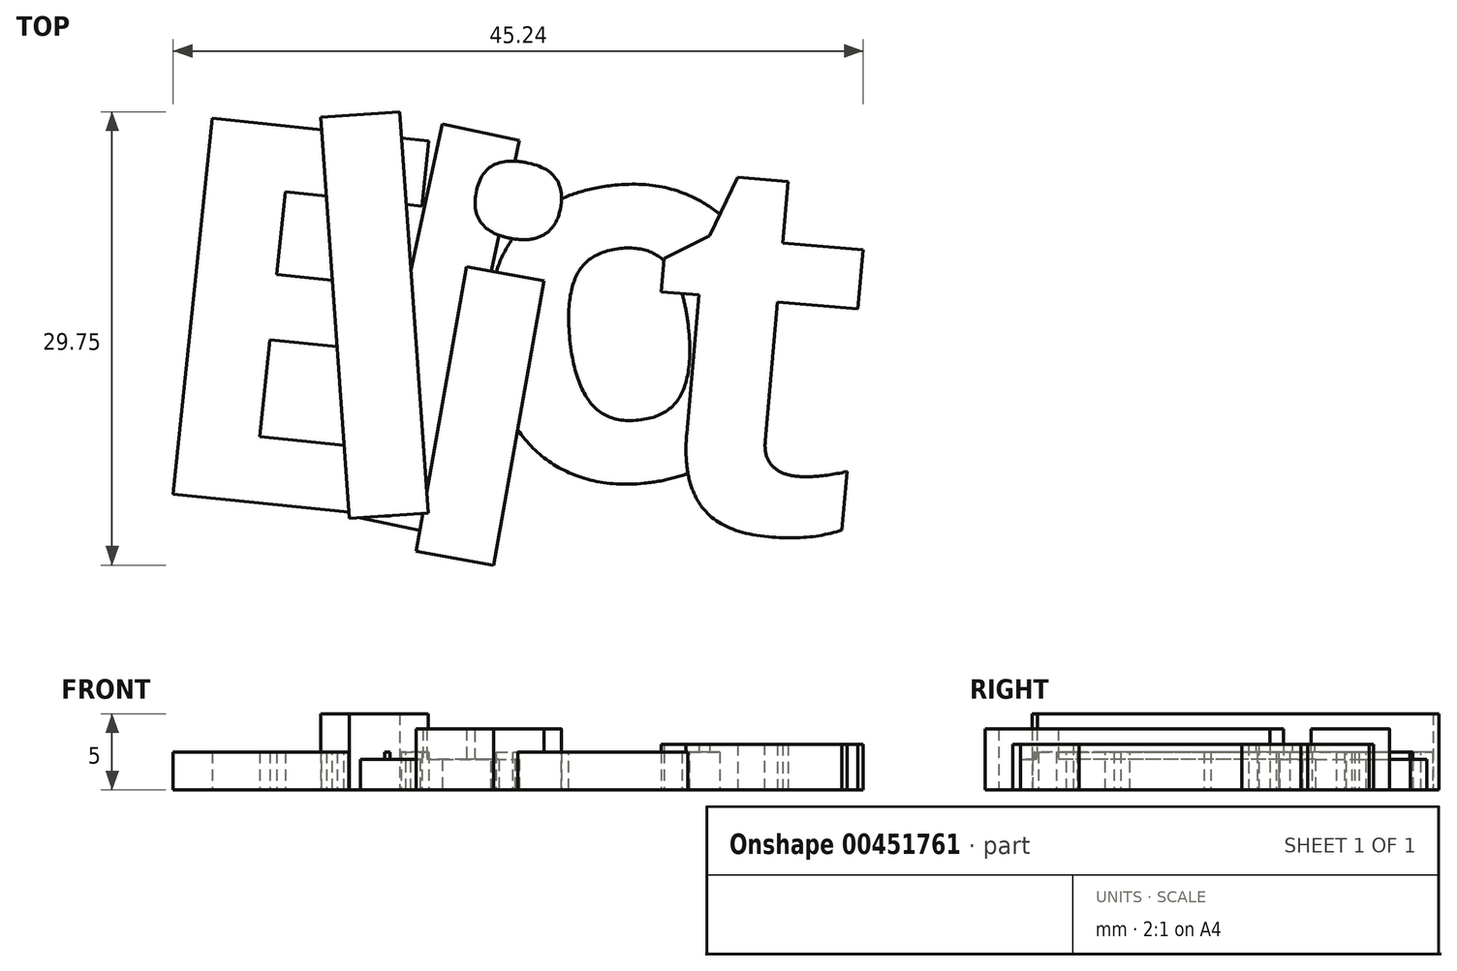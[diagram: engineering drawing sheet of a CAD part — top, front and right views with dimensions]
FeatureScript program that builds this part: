
annotation { "Feature Type Name" : "Feature", "Feature Type Description" : "" }
export const myFeature = defineFeature(function(context is Context, id is Id, definition is map)
    precondition{}
    {
        {
            var Q0;
            Q0=qCreatedBy(makeId("Top.planeOp"),FACE);
            var sketch = newSketch(context, id + "F0", { "sketchPlane" : qUnion([Q0])});
            skText(sketch, "E0", { "text": "E", "fontName": "OpenSans-Bold.ttf"});
            skText(sketch, "E1", { "text": "l", "fontName": "OpenSans-Bold.ttf"});
            skText(sketch, "E2", { "text": "i", "fontName": "OpenSans-Bold.ttf"});
            skText(sketch, "E3", { "text": "o", "fontName": "OpenSans-Bold.ttf"});
            skText(sketch, "E4", { "text": "t", "fontName": "OpenSans-Bold.ttf"});
            skLineSegment(sketch, "E5", {"start": v(-42.9, 49.18) * mm, "end": v(-72.08, 8.9) * mm, "construction": true});
            skLineSegment(sketch, "E6", {"start": v(-42.9, 49.18) * mm, "end": v(-73, 49.18) * mm, "construction": true});
            skText(sketch, "E7", { "text": "l", "fontName": "OpenSans-Bold.ttf"});
            const initialGuessF0  = {"E0": [-0.05238, -0.0083, 0.99466, -0.10322, 0.025], "E1": [-0.04043, -0.01042, 0.99747, 0.07107, 0.025], "E2": [-0.03602, -0.01192, 0.9848, -0.17365, 0.025], "E3": [-0.02907, -0.00869, 0.99452, 0.10453, 0.025], "E4": [-0.01939, -0.01029, 0.9962, -0.08716, 0.025], "E7": [-0.03979, -0.00958, 0.97815, -0.20791, 0.025]};
            skSetInitialGuess(sketch, initialGuessF0);
            skSolve(sketch);
        }
        {
            var Q0;
            {var subQ11=sQuery(id+"F0.wireOp",EDGE,"E0.sketch_text.stroke-1");Q0=makeQuery(id+"F0.imprint","IMPRINT",FACE,{"disambiguationData":[TD([[makeQuery(id+"F0.imprint","IMPRINT",EDGE,{"derivedFrom":subQ11}),-1.0]])]});}
            var Q1;
            {var subQ3=sQuery(id+"F0.wireOp",EDGE,"E1.sketch_text.stroke-3");var subQ9=sQuery(id+"F0.wireOp",EDGE,"E0.sketch_text.stroke-0");var subQ11=makeQuery(id+"F0.imprint","INTERSECT",VERTEX,{"derivedFrom":[subQ9,subQ3]});Q1=makeQuery(id+"F0.imprint","IMPRINT",FACE,{"disambiguationData":[TD([[makeQuery(id+"F0.imprint","IMPRINT",EDGE,{"disambiguationData":[TD([[subQ11,-1.0]])],"derivedFrom":subQ9}),-1.0]])]});}
            var Q2;
            {var subQ0=sQuery(id+"F0.wireOp",EDGE,"E0.sketch_text.stroke-7");Q2=makeQuery(id+"F0.imprint","IMPRINT",FACE,{"disambiguationData":[TD([[makeQuery(id+"F0.imprint","IMPRINT",EDGE,{"derivedFrom":subQ0}),-1.0]])]});}
            var Q3;
            {var subQ0=sQuery(id+"F0.wireOp",EDGE,"E0.sketch_text.stroke-3");Q3=makeQuery(id+"F0.imprint","IMPRINT",FACE,{"disambiguationData":[TD([[makeQuery(id+"F0.imprint","IMPRINT",EDGE,{"derivedFrom":subQ0}),-1.0]])]});}
            var Q4;
            {var subQ0=sQuery(id+"F0.wireOp",EDGE,"E1.sketch_text.stroke-1");var subQ1=sQuery(id+"F0.wireOp",EDGE,"E0.sketch_text.stroke-2");var subQ2=makeQuery(id+"F0.imprint","INTERSECT",VERTEX,{"derivedFrom":[subQ1,subQ0]});Q4=makeQuery(id+"F0.imprint","IMPRINT",FACE,{"disambiguationData":[TD([[makeQuery(id+"F0.imprint","IMPRINT",EDGE,{"disambiguationData":[TD([[subQ2,-1.0]])],"derivedFrom":subQ1}),-1.0]])]});}
            var Q5;
            {var subQ5=sQuery(id+"F0.wireOp",EDGE,"E0.sketch_text.stroke-7");var subQ7=sQuery(id+"F0.wireOp",EDGE,"E0.sketch_text.stroke-6");var subQ8=makeQuery(id+"F0.imprint","INTERSECT",VERTEX,{"derivedFrom":[subQ7,subQ5]});Q5=makeQuery(id+"F0.imprint","IMPRINT",FACE,{"disambiguationData":[TD([[makeQuery(id+"F0.imprint","IMPRINT",EDGE,{"disambiguationData":[TD([[subQ8,1.0]])],"derivedFrom":subQ7}),-1.0]])]});}
            var Q6;
            {var subQ0=sQuery(id+"F0.wireOp",EDGE,"E1.sketch_text.stroke-1");var subQ1=sQuery(id+"F0.wireOp",EDGE,"E0.sketch_text.stroke-0");var subQ2=makeQuery(id+"F0.imprint","INTERSECT",VERTEX,{"derivedFrom":[subQ1,subQ0]});Q6=makeQuery(id+"F0.imprint","IMPRINT",FACE,{"disambiguationData":[TD([[makeQuery(id+"F0.imprint","IMPRINT",EDGE,{"disambiguationData":[TD([[subQ2,1.0]])],"derivedFrom":subQ1}),-1.0]])]});}
            var Q7;
            {var subQ3=sQuery(id+"F0.wireOp",EDGE,"E1.sketch_text.stroke-0");var subQ5=sQuery(id+"F0.wireOp",EDGE,"E0.sketch_text.stroke-0");var subQ6=makeQuery(id+"F0.imprint","INTERSECT",VERTEX,{"derivedFrom":[subQ5,subQ3]});Q7=makeQuery(id+"F0.imprint","IMPRINT",FACE,{"disambiguationData":[TD([[makeQuery(id+"F0.imprint","IMPRINT",EDGE,{"disambiguationData":[TD([[subQ6,-1.0]])],"derivedFrom":subQ5}),-1.0]])]});}
            extrude(context, id + "F1", {"entities" : qUnion([Q0, Q1, Q2, Q3, Q4, Q5, Q6, Q7]), "depth" : 2.5 * mm, "offsetDistance" : 25 * mm});
        }
        {
            var Q0;
            {var subQ9=sQuery(id+"F0.wireOp",EDGE,"E1.sketch_text.stroke-1");Q0=makeQuery(id+"F0.imprint","IMPRINT",FACE,{"disambiguationData":[TD([[makeQuery(id+"F0.imprint","IMPRINT",EDGE,{"derivedFrom":subQ9}),-1.0]])]});}
            var Q1;
            {var subQ0=sQuery(id+"F0.wireOp",EDGE,"E1.sketch_text.stroke-3");var subQ1=sQuery(id+"F0.wireOp",EDGE,"E0.sketch_text.stroke-0");var subQ2=makeQuery(id+"F0.imprint","INTERSECT",VERTEX,{"derivedFrom":[subQ1,subQ0]});Q1=makeQuery(id+"F0.imprint","IMPRINT",FACE,{"disambiguationData":[TD([[makeQuery(id+"F0.imprint","IMPRINT",EDGE,{"disambiguationData":[TD([[subQ2,-1.0]])],"derivedFrom":subQ1}),1.0]])]});}
            var Q2;
            {var subQ0=sQuery(id+"F0.wireOp",EDGE,"E1.sketch_text.stroke-3");var subQ1=sQuery(id+"F0.wireOp",EDGE,"E1.sketch_text.stroke-2");var subQ2=makeQuery(id+"F0.imprint","INTERSECT",VERTEX,{"derivedFrom":[subQ1,subQ0]});Q2=makeQuery(id+"F0.imprint","IMPRINT",FACE,{"disambiguationData":[TD([[makeQuery(id+"F0.imprint","IMPRINT",EDGE,{"disambiguationData":[TD([[subQ2,1.0]])],"derivedFrom":subQ1}),-1.0]])]});}
            var Q3;
            {var subQ0=sQuery(id+"F0.wireOp",EDGE,"E0.sketch_text.stroke-7");Q3=makeQuery(id+"F0.imprint","IMPRINT",FACE,{"disambiguationData":[TD([[makeQuery(id+"F0.imprint","IMPRINT",EDGE,{"derivedFrom":subQ0}),-1.0]])]});}
            var Q4;
            {var subQ5=sQuery(id+"F0.wireOp",EDGE,"E0.sketch_text.stroke-4");var subQ9=sQuery(id+"F0.wireOp",EDGE,"E1.sketch_text.stroke-3");var subQ10=makeQuery(id+"F0.imprint","INTERSECT",VERTEX,{"derivedFrom":[subQ5,subQ9]});Q4=makeQuery(id+"F0.imprint","IMPRINT",FACE,{"disambiguationData":[TD([[makeQuery(id+"F0.imprint","IMPRINT",EDGE,{"disambiguationData":[TD([[subQ10,-1.0]])],"derivedFrom":subQ5}),1.0]])]});}
            var Q5;
            {var subQ5=sQuery(id+"F0.wireOp",EDGE,"E0.sketch_text.stroke-7");var subQ7=sQuery(id+"F0.wireOp",EDGE,"E0.sketch_text.stroke-6");var subQ8=makeQuery(id+"F0.imprint","INTERSECT",VERTEX,{"derivedFrom":[subQ7,subQ5]});Q5=makeQuery(id+"F0.imprint","IMPRINT",FACE,{"disambiguationData":[TD([[makeQuery(id+"F0.imprint","IMPRINT",EDGE,{"disambiguationData":[TD([[subQ8,1.0]])],"derivedFrom":subQ7}),-1.0]])]});}
            var Q6;
            {var subQ11=sQuery(id+"F0.wireOp",EDGE,"E0.sketch_text.stroke-8");var subQ12=sQuery(id+"F0.wireOp",EDGE,"E0.sketch_text.stroke-7");var subQ13=makeQuery(id+"F0.imprint","INTERSECT",VERTEX,{"derivedFrom":[subQ12,subQ11]});Q6=makeQuery(id+"F0.imprint","IMPRINT",FACE,{"disambiguationData":[TD([[makeQuery(id+"F0.imprint","IMPRINT",EDGE,{"disambiguationData":[TD([[subQ13,1.0]])],"derivedFrom":subQ12}),1.0]])]});}
            var Q7;
            {var subQ3=sQuery(id+"F0.wireOp",EDGE,"E1.sketch_text.stroke-0");var subQ5=sQuery(id+"F0.wireOp",EDGE,"E0.sketch_text.stroke-0");var subQ6=makeQuery(id+"F0.imprint","INTERSECT",VERTEX,{"derivedFrom":[subQ5,subQ3]});Q7=makeQuery(id+"F0.imprint","IMPRINT",FACE,{"disambiguationData":[TD([[makeQuery(id+"F0.imprint","IMPRINT",EDGE,{"disambiguationData":[TD([[subQ6,-1.0]])],"derivedFrom":subQ5}),-1.0]])]});}
            var Q8;
            {var subQ5=sQuery(id+"F0.wireOp",EDGE,"E1.sketch_text.stroke-1");var subQ7=sQuery(id+"F0.wireOp",EDGE,"E0.sketch_text.stroke-0");var subQ8=makeQuery(id+"F0.imprint","INTERSECT",VERTEX,{"derivedFrom":[subQ7,subQ5]});Q8=makeQuery(id+"F0.imprint","IMPRINT",FACE,{"disambiguationData":[TD([[makeQuery(id+"F0.imprint","IMPRINT",EDGE,{"disambiguationData":[TD([[subQ8,1.0]])],"derivedFrom":subQ7}),1.0]])]});}
            var Q9;
            {var subQ0=sQuery(id+"F0.wireOp",EDGE,"E1.sketch_text.stroke-3");var subQ1=sQuery(id+"F0.wireOp",EDGE,"E1.sketch_text.stroke-0");var subQ2=makeQuery(id+"F0.imprint","INTERSECT",VERTEX,{"derivedFrom":[subQ1,subQ0]});Q9=makeQuery(id+"F0.imprint","IMPRINT",FACE,{"disambiguationData":[TD([[makeQuery(id+"F0.imprint","IMPRINT",EDGE,{"disambiguationData":[TD([[subQ2,-1.0]])],"derivedFrom":subQ1}),-1.0]])]});}
            extrude(context, id + "F2", {"entities" : qUnion([Q0, Q1, Q2, Q3, Q4, Q5, Q6, Q7, Q8, Q9]), "operationType" : NewBodyOperationType.ADD, "depth" : 3 * mm, "offsetDistance" : 25 * mm});
        }
        {
            var Q0;
            {var subQ0=sQuery(id+"F0.wireOp",EDGE,"E7.sketch_text.stroke-2");Q0=makeQuery(id+"F0.imprint","IMPRINT",FACE,{"disambiguationData":[TD([[makeQuery(id+"F0.imprint","IMPRINT",EDGE,{"derivedFrom":subQ0}),-1.0]])]});}
            var Q1;
            {var subQ0=sQuery(id+"F0.wireOp",EDGE,"E2.sketch_text.stroke-7");var subQ1=sQuery(id+"F0.wireOp",EDGE,"E2.sketch_text.stroke-6");var subQ2=makeQuery(id+"F0.imprint","INTERSECT",VERTEX,{"derivedFrom":[subQ1,subQ0]});Q1=makeQuery(id+"F0.imprint","IMPRINT",FACE,{"disambiguationData":[TD([[makeQuery(id+"F0.imprint","IMPRINT",EDGE,{"disambiguationData":[TD([[subQ2,1.0]])],"derivedFrom":subQ1}),-1.0]])]});}
            var Q2;
            Q2=makeQuery(id+"F2.opExtrude","CAP_FACE",FACE,{"disambiguationData":[OSD([sQuery(id+"F0.wireOp",EDGE,"E0.sketch_text.stroke-2"),sQuery(id+"F0.wireOp",EDGE,"E0.sketch_text.stroke-3"),sQuery(id+"F0.wireOp",EDGE,"E0.sketch_text.stroke-4"),sQuery(id+"F0.wireOp",EDGE,"E0.sketch_text.stroke-6"),sQuery(id+"F0.wireOp",EDGE,"E0.sketch_text.stroke-7"),sQuery(id+"F0.wireOp",EDGE,"E0.sketch_text.stroke-8"),sQuery(id+"F0.wireOp",EDGE,"E0.sketch_text.stroke-10"),sQuery(id+"F0.wireOp",EDGE,"E0.sketch_text.stroke-11"),sQuery(id+"F0.wireOp",EDGE,"E1.sketch_text.stroke-1"),sQuery(id+"F0.wireOp",EDGE,"E1.sketch_text.stroke-2"),sQuery(id+"F0.wireOp",EDGE,"E1.sketch_text.stroke-3")])],"isStart":false});
            var Q3;
            {var subQ0=sQuery(id+"F0.wireOp",EDGE,"E2.sketch_text.stroke-4");var subQ1=sQuery(id+"F0.wireOp",EDGE,"E2.sketch_text.stroke-0");var subQ2=makeQuery(id+"F0.imprint","INTERSECT",VERTEX,{"derivedFrom":[subQ1,subQ0]});Q3=makeQuery(id+"F0.imprint","IMPRINT",FACE,{"disambiguationData":[TD([[makeQuery(id+"F0.imprint","IMPRINT",EDGE,{"disambiguationData":[TD([[subQ2,-1.0]])],"derivedFrom":subQ1}),-1.0]])]});}
            var Q4;
            {var subQ3=sQuery(id+"F0.wireOp",EDGE,"E0.sketch_text.stroke-0");var subQ5=sQuery(id+"F0.wireOp",EDGE,"E0.sketch_text.stroke-11");var subQ9=makeQuery(id+"F0.imprint","INTERSECT",VERTEX,{"derivedFrom":[subQ3,subQ5]});Q4=makeQuery(id+"F0.imprint","IMPRINT",FACE,{"disambiguationData":[TD([[makeQuery(id+"F0.imprint","IMPRINT",EDGE,{"disambiguationData":[TD([[subQ9,-1.0]])],"derivedFrom":subQ3}),1.0]])]});}
            var Q5;
            {var subQ11=sQuery(id+"F0.wireOp",EDGE,"E0.sketch_text.stroke-8");var subQ12=sQuery(id+"F0.wireOp",EDGE,"E0.sketch_text.stroke-7");var subQ13=makeQuery(id+"F0.imprint","INTERSECT",VERTEX,{"derivedFrom":[subQ12,subQ11]});Q5=makeQuery(id+"F0.imprint","IMPRINT",FACE,{"disambiguationData":[TD([[makeQuery(id+"F0.imprint","IMPRINT",EDGE,{"disambiguationData":[TD([[subQ13,1.0]])],"derivedFrom":subQ12}),1.0]])]});}
            var Q6;
            {var subQ0=sQuery(id+"F0.wireOp",EDGE,"E0.sketch_text.stroke-8");var subQ1=sQuery(id+"F0.wireOp",EDGE,"E0.sketch_text.stroke-7");var subQ2=makeQuery(id+"F0.imprint","INTERSECT",VERTEX,{"derivedFrom":[subQ1,subQ0]});Q6=makeQuery(id+"F0.imprint","IMPRINT",FACE,{"disambiguationData":[TD([[makeQuery(id+"F0.imprint","IMPRINT",EDGE,{"disambiguationData":[TD([[subQ2,1.0]])],"derivedFrom":subQ1}),-1.0]])]});}
            extrude(context, id + "F3", {"entities" : qUnion([Q0, Q1, Q2, Q3, Q4, Q5, Q6]), "operationType" : NewBodyOperationType.ADD, "depth" : 2 * mm, "offsetDistance" : 25 * mm});
        }
        {
            var Q0;
            {var subQ1=sQuery(id+"F0.wireOp",EDGE,"E2.sketch_text.stroke-5");Q0=makeQuery(id+"F0.imprint","IMPRINT",FACE,{"disambiguationData":[TD([[makeQuery(id+"F0.imprint","IMPRINT",EDGE,{"derivedFrom":subQ1}),-1.0]])]});}
            var Q1;
            {var subQ1=sQuery(id+"F0.wireOp",EDGE,"E2.sketch_text.stroke-1");Q1=makeQuery(id+"F0.imprint","IMPRINT",FACE,{"disambiguationData":[TD([[makeQuery(id+"F0.imprint","IMPRINT",EDGE,{"derivedFrom":subQ1}),-1.0]])]});}
            var Q2;
            {var subQ0=sQuery(id+"F0.wireOp",EDGE,"E2.sketch_text.stroke-3");var subQ1=sQuery(id+"F0.wireOp",EDGE,"E2.sketch_text.stroke-2");var subQ2=makeQuery(id+"F0.imprint","INTERSECT",VERTEX,{"derivedFrom":[subQ1,subQ0]});Q2=makeQuery(id+"F0.imprint","IMPRINT",FACE,{"disambiguationData":[TD([[makeQuery(id+"F0.imprint","IMPRINT",EDGE,{"disambiguationData":[TD([[subQ2,1.0]])],"derivedFrom":subQ1}),-1.0]])]});}
            var Q3;
            {var subQ0=sQuery(id+"F0.wireOp",EDGE,"E2.sketch_text.stroke-4");var subQ1=sQuery(id+"F0.wireOp",EDGE,"E2.sketch_text.stroke-0");var subQ2=makeQuery(id+"F0.imprint","INTERSECT",VERTEX,{"derivedFrom":[subQ1,subQ0]});Q3=makeQuery(id+"F0.imprint","IMPRINT",FACE,{"disambiguationData":[TD([[makeQuery(id+"F0.imprint","IMPRINT",EDGE,{"disambiguationData":[TD([[subQ2,-1.0]])],"derivedFrom":subQ1}),-1.0]])]});}
            var Q4;
            {var subQ0=sQuery(id+"F0.wireOp",EDGE,"E2.sketch_text.stroke-7");var subQ1=sQuery(id+"F0.wireOp",EDGE,"E2.sketch_text.stroke-6");var subQ2=makeQuery(id+"F0.imprint","INTERSECT",VERTEX,{"derivedFrom":[subQ1,subQ0]});Q4=makeQuery(id+"F0.imprint","IMPRINT",FACE,{"disambiguationData":[TD([[makeQuery(id+"F0.imprint","IMPRINT",EDGE,{"disambiguationData":[TD([[subQ2,1.0]])],"derivedFrom":subQ1}),-1.0]])]});}
            var Q5;
            {var subQ0=sQuery(id+"F0.wireOp",EDGE,"E2.sketch_text.stroke-8");var subQ1=sQuery(id+"F0.wireOp",EDGE,"E2.sketch_text.stroke-7");var subQ2=makeQuery(id+"F0.imprint","INTERSECT",VERTEX,{"derivedFrom":[subQ1,subQ0]});Q5=makeQuery(id+"F0.imprint","IMPRINT",FACE,{"disambiguationData":[TD([[makeQuery(id+"F0.imprint","IMPRINT",EDGE,{"disambiguationData":[TD([[subQ2,1.0]])],"derivedFrom":subQ1}),-1.0]])]});}
            var Q6;
            {var subQ5=sQuery(id+"F0.wireOp",EDGE,"E2.sketch_text.stroke-1");var subQ6=sQuery(id+"F0.wireOp",EDGE,"E2.sketch_text.stroke-0");var subQ7=makeQuery(id+"F0.imprint","INTERSECT",VERTEX,{"derivedFrom":[subQ6,subQ5]});Q6=makeQuery(id+"F0.imprint","IMPRINT",FACE,{"disambiguationData":[TD([[makeQuery(id+"F0.imprint","IMPRINT",EDGE,{"disambiguationData":[TD([[subQ7,1.0]])],"derivedFrom":subQ6}),-1.0]])]});}
            extrude(context, id + "F4", {"entities" : qUnion([Q0, Q1, Q2, Q3, Q4, Q5, Q6]), "operationType" : NewBodyOperationType.ADD, "depth" : 4 * mm, "offsetDistance" : 25 * mm});
        }
        {
            var Q0;
            {var subQ0=sQuery(id+"F0.wireOp",EDGE,"E3.sketch_text.stroke-16");Q0=makeQuery(id+"F0.imprint","IMPRINT",FACE,{"disambiguationData":[TD([[makeQuery(id+"F0.imprint","IMPRINT",EDGE,{"derivedFrom":subQ0}),-1.0]])]});}
            var Q1;
            Q1=makeQuery(id+"F0.imprint","IMPRINT",FACE,{"disambiguationData":[TD([[makeQuery(id+"F0.imprint","IMPRINT",EDGE,{"derivedFrom":sQuery(id+"F0.wireOp",EDGE,"E3.sketch_text.stroke-0")}),-1.0]])]});
            var Q2;
            {var subQ0=sQuery(id+"F0.wireOp",EDGE,"E2.sketch_text.stroke-8");var subQ1=sQuery(id+"F0.wireOp",EDGE,"E2.sketch_text.stroke-7");var subQ2=makeQuery(id+"F0.imprint","INTERSECT",VERTEX,{"derivedFrom":[subQ1,subQ0]});Q2=makeQuery(id+"F0.imprint","IMPRINT",FACE,{"disambiguationData":[TD([[makeQuery(id+"F0.imprint","IMPRINT",EDGE,{"disambiguationData":[TD([[subQ2,1.0]])],"derivedFrom":subQ1}),-1.0]])]});}
            var Q3;
            {var subQ0=sQuery(id+"F0.wireOp",EDGE,"E2.sketch_text.stroke-3");var subQ1=sQuery(id+"F0.wireOp",EDGE,"E2.sketch_text.stroke-2");var subQ2=makeQuery(id+"F0.imprint","INTERSECT",VERTEX,{"derivedFrom":[subQ1,subQ0]});Q3=makeQuery(id+"F0.imprint","IMPRINT",FACE,{"disambiguationData":[TD([[makeQuery(id+"F0.imprint","IMPRINT",EDGE,{"disambiguationData":[TD([[subQ2,1.0]])],"derivedFrom":subQ1}),-1.0]])]});}
            extrude(context, id + "F5", {"entities" : qUnion([Q0, Q1, Q2, Q3]), "operationType" : NewBodyOperationType.ADD, "depth" : 2.5 * mm, "offsetDistance" : 25 * mm});
        }
        {
            var Q0;
            {var subQ8=sQuery(id+"F0.wireOp",EDGE,"E3.sketch_text.stroke-8");Q0=makeQuery(id+"F0.imprint","IMPRINT",FACE,{"disambiguationData":[TD([[makeQuery(id+"F0.imprint","IMPRINT",EDGE,{"derivedFrom":subQ8}),1.0]])]});}
            var Q1;
            {var subQ6=sQuery(id+"F0.wireOp",EDGE,"E3.sketch_text.stroke-8");Q1=makeQuery(id+"F0.imprint","IMPRINT",FACE,{"disambiguationData":[TD([[makeQuery(id+"F0.imprint","IMPRINT",EDGE,{"derivedFrom":subQ6}),-1.0]])]});}
            var Q2;
            {var subQ0=sQuery(id+"F0.wireOp",EDGE,"E3.sketch_text.stroke-5");var subQ1=sQuery(id+"F0.wireOp",EDGE,"E3.sketch_text.stroke-4");var subQ2=makeQuery(id+"F0.imprint","INTERSECT",VERTEX,{"derivedFrom":[subQ1,subQ0]});Q2=makeQuery(id+"F0.imprint","IMPRINT",FACE,{"disambiguationData":[TD([[makeQuery(id+"F0.imprint","IMPRINT",EDGE,{"disambiguationData":[TD([[subQ2,1.0]])],"derivedFrom":subQ1}),1.0]])]});}
            extrude(context, id + "F6", {"entities" : qUnion([Q0, Q1, Q2]), "operationType" : NewBodyOperationType.ADD, "depth" : 3 * mm, "offsetDistance" : 25 * mm});
        }
    });
